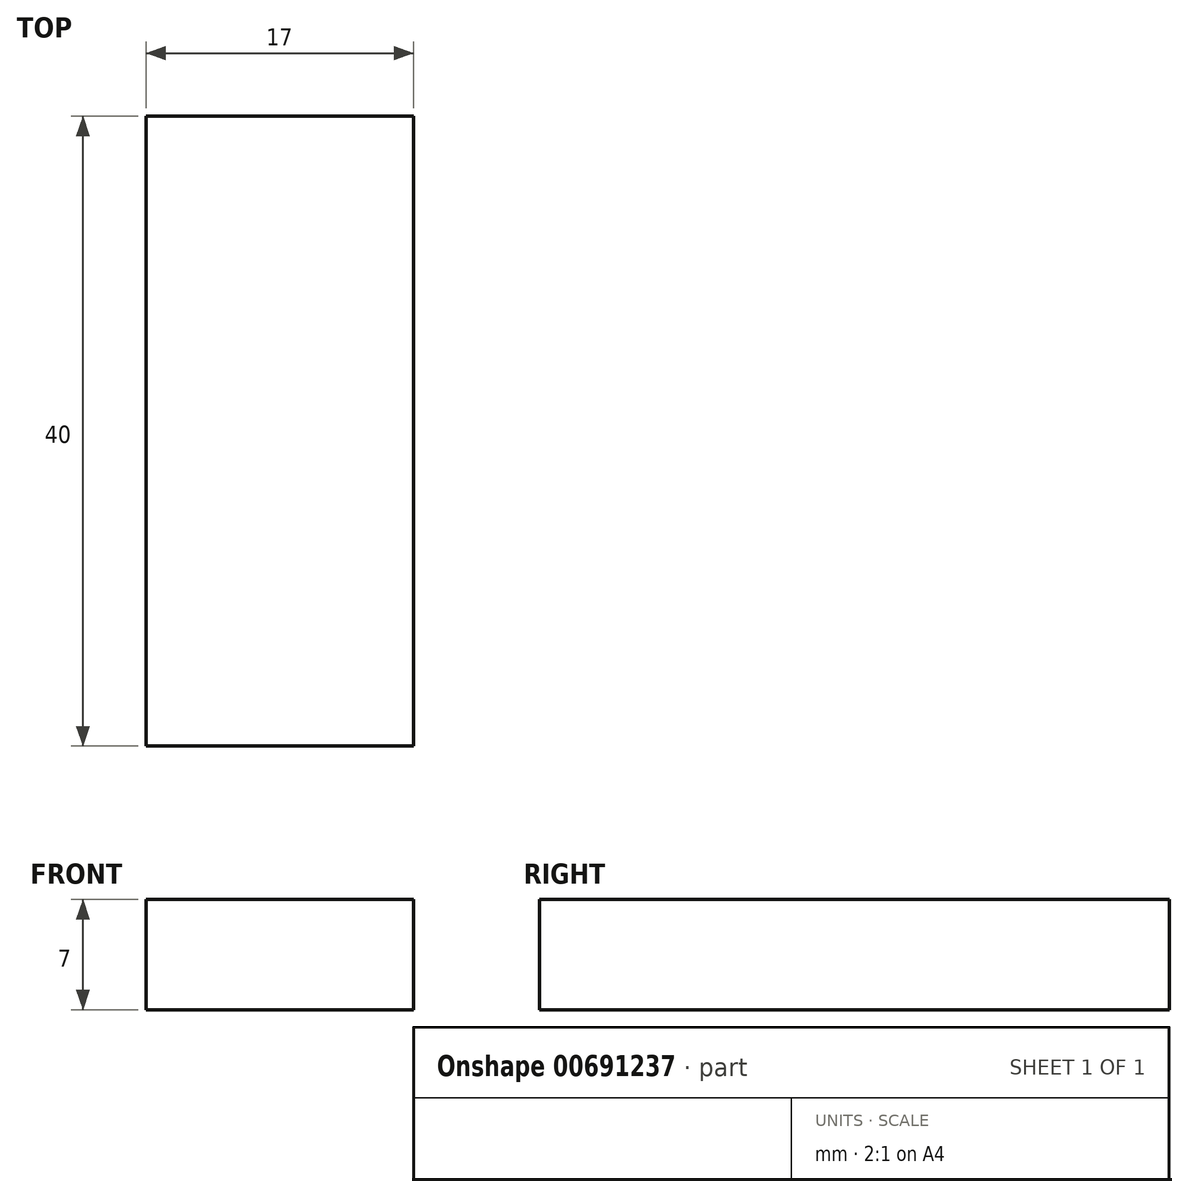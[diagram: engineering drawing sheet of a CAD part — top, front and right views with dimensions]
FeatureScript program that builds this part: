
annotation { "Feature Type Name" : "Feature", "Feature Type Description" : "" }
export const myFeature = defineFeature(function(context is Context, id is Id, definition is map)
    precondition{}
    {
        {
            var Q0;
            Q0=qCreatedBy(makeId("Top.planeOp"),FACE);
            var sketch = newSketch(context, id + "F0", { "sketchPlane" : qUnion([Q0])});
            skLineSegment(sketch, "E0.bottom", {"start": v(8.5, 20) * mm, "end": v(-8.5, 20) * mm});
            skLineSegment(sketch, "E0.top", {"start": v(8.5, -20) * mm, "end": v(-8.5, -20) * mm});
            skLineSegment(sketch, "E0.left", {"start": v(8.5, 20) * mm, "end": v(8.5, -20) * mm});
            skLineSegment(sketch, "E0.right", {"start": v(-8.5, 20) * mm, "end": v(-8.5, -20) * mm});
            skPoint(sketch, "E0.middle", {"position": v(0, 0) * mm});
            skSolve(sketch);
        }
        {
            var Q0;
            Q0=qSketchRegion(id+"F0",true);
            extrude(context, id + "F1", {"entities" : qUnion([Q0]), "depth" : 7 * mm, "offsetDistance" : 25 * mm});
        }
    });
